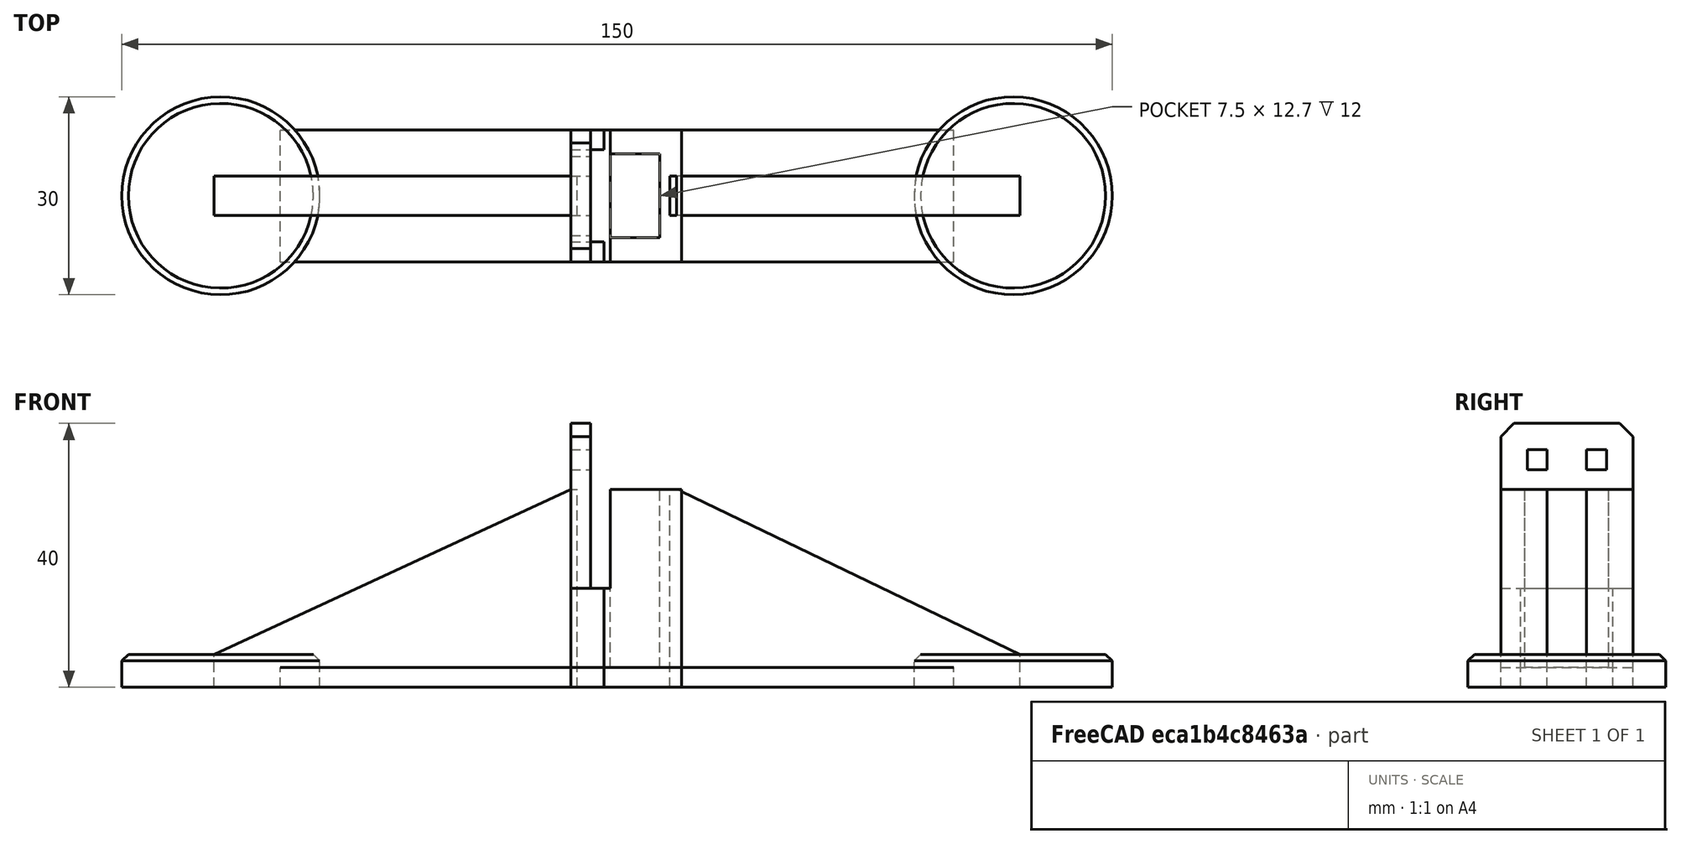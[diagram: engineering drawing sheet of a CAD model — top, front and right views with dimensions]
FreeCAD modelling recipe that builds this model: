
FCSTD DOCUMENT  (FreeCAD 0.18R16146 (Git))
Label: 3mm-sheet-stand
License: All rights reserved
LicenseURL: http://en.wikipedia.org/wiki/All_rights_reserved
objects: Part::Box×10, Part::Chamfer×5, Part::Cut×3, Part::Cylinder×2, Part::MultiFuse×2, Part::Feature×1
note: 23 computed .brp shape members not serialized (recipe doc carries the construction recipe); baked Part::Feature solids carry a one-line shape summary decoded from their .brp

FEATURE [Part::Feature] Box001  label="Cube001"
  Placement = pos=(7,-1.6e-15,0) rot=(0,0,1;4.71239rad)
  shape: bbox 7.5 x 12.7 x 27 mm, 6 faces (baked)
FEATURE [Part::Box] Box  label="Cube"
  AttacherType = Attacher::AttachEngine3D
  Height = 30
  Length = 14
  Placement = pos=(0,-10,0) rot=(0,0,1;0rad)
  Width = 20
FEATURE [Part::Cut] Cut
  Base = -> Box
  Placement = pos=(-4.25,0,0) rot=(0,0,1;0rad)
  Tool = -> Box001
FEATURE [Part::Cylinder] Cylinder
  Angle = 360
  AttacherType = Attacher::AttachEngine3D
  Height = 5
  Placement = pos=(-35,0,0) rot=(0,0,1;0rad)
  Radius = 15
FEATURE [Part::Cylinder] Cylinder001
  Angle = 360
  AttacherType = Attacher::AttachEngine3D
  Height = 5
  Placement = pos=(35,0,0) rot=(0,0,1;0rad)
  Radius = 15
FEATURE [Part::Box] Box002  label="Cube002"
  AttacherType = Attacher::AttachEngine3D
  Height = 40
  Length = 3
  Placement = pos=(-7,-10,0) rot=(0,0,1;0rad)
  Width = 20
FEATURE [Part::Box] Box003  label="Cube003"
  AttacherType = Attacher::AttachEngine3D
  Height = 3
  Length = 102
  Placement = pos=(-51,-10,0) rot=(0,0,1;0rad)
  Width = 20
FEATURE [Part::Box] Box004  label="Cube004"
  AttacherType = Attacher::AttachEngine3D
  Height = 30
  Length = 55
  Placement = pos=(-61,-3,0) rot=(0,0,1;0rad)
  Width = 6
FEATURE [Part::Box] Box005  label="Cube005"
  AttacherType = Attacher::AttachEngine3D
  Height = 30
  Length = 53
  Placement = pos=(8,-3,0) rot=(0,0,1;0rad)
  Width = 6
FEATURE [Part::Box] Box006  label="Cube006"
  AttacherType = Attacher::AttachEngine3D
  Height = 15
  Length = 5
  Placement = pos=(-7,-10,0) rot=(0,0,1;0rad)
  Width = 3
FEATURE [Part::Box] Box007  label="Cube007"
  AttacherType = Attacher::AttachEngine3D
  Height = 15
  Length = 5
  Placement = pos=(-7,7,0) rot=(0,0,1;0rad)
  Width = 3
FEATURE [Part::Box] Box008  label="Cube008"
  AttacherType = Attacher::AttachEngine3D
  Height = 20
  Length = 3
  Placement = pos=(-4,-10,15) rot=(0,0,1;0rad)
  Width = 20
FEATURE [Part::MultiFuse] Fusion
  Shapes = -> [Cut,Box002]
FEATURE [Part::Cut] Cut001
  Base = -> Fusion
  Tool = -> Box008
FEATURE [Part::Chamfer] Chamfer002
  Base = -> Cylinder
  Edges = 1 edges r=1: [Edge1]
  Placement = pos=(-25,0,0) rot=(0,0,1;0rad)
FEATURE [Part::Chamfer] Chamfer003
  Base = -> Cylinder001
  Edges = 1 edges r=1: [Edge1]
  Placement = pos=(25,0,0) rot=(0,0,1;0rad)
FEATURE [Part::Box] Box009  label="Cube009"
  AttacherType = Attacher::AttachEngine3D
  Height = 3
  Length = 10
  Placement = pos=(-7,-6,33) rot=(0,0,1;0rad)
  Width = 3
FEATURE [Part::Box] Box010  label="Cube010"
  AttacherType = Attacher::AttachEngine3D
  Height = 3
  Length = 10
  Placement = pos=(-7,3,33) rot=(0,0,1;0rad)
  Width = 3
FEATURE [Part::MultiFuse] Fusion001
  Shapes = -> [Box009,Box010]
FEATURE [Part::Cut] Cut002
  Base = -> Cut001
  Tool = -> Fusion001
FEATURE [Part::Chamfer] Chamfer004
  Base = -> Cut002
  Edges = 2 edges r=2: [Edge18,Edge19]
FEATURE [Part::Chamfer] Chamfer
  Base = -> Box004
  Edges = 1 edges: [Edge2 r1=25 r2=54]
FEATURE [Part::Chamfer] Chamfer005
  Base = -> Box005
  Edges = 1 edges: [Edge6 r1=25 r2=52]
